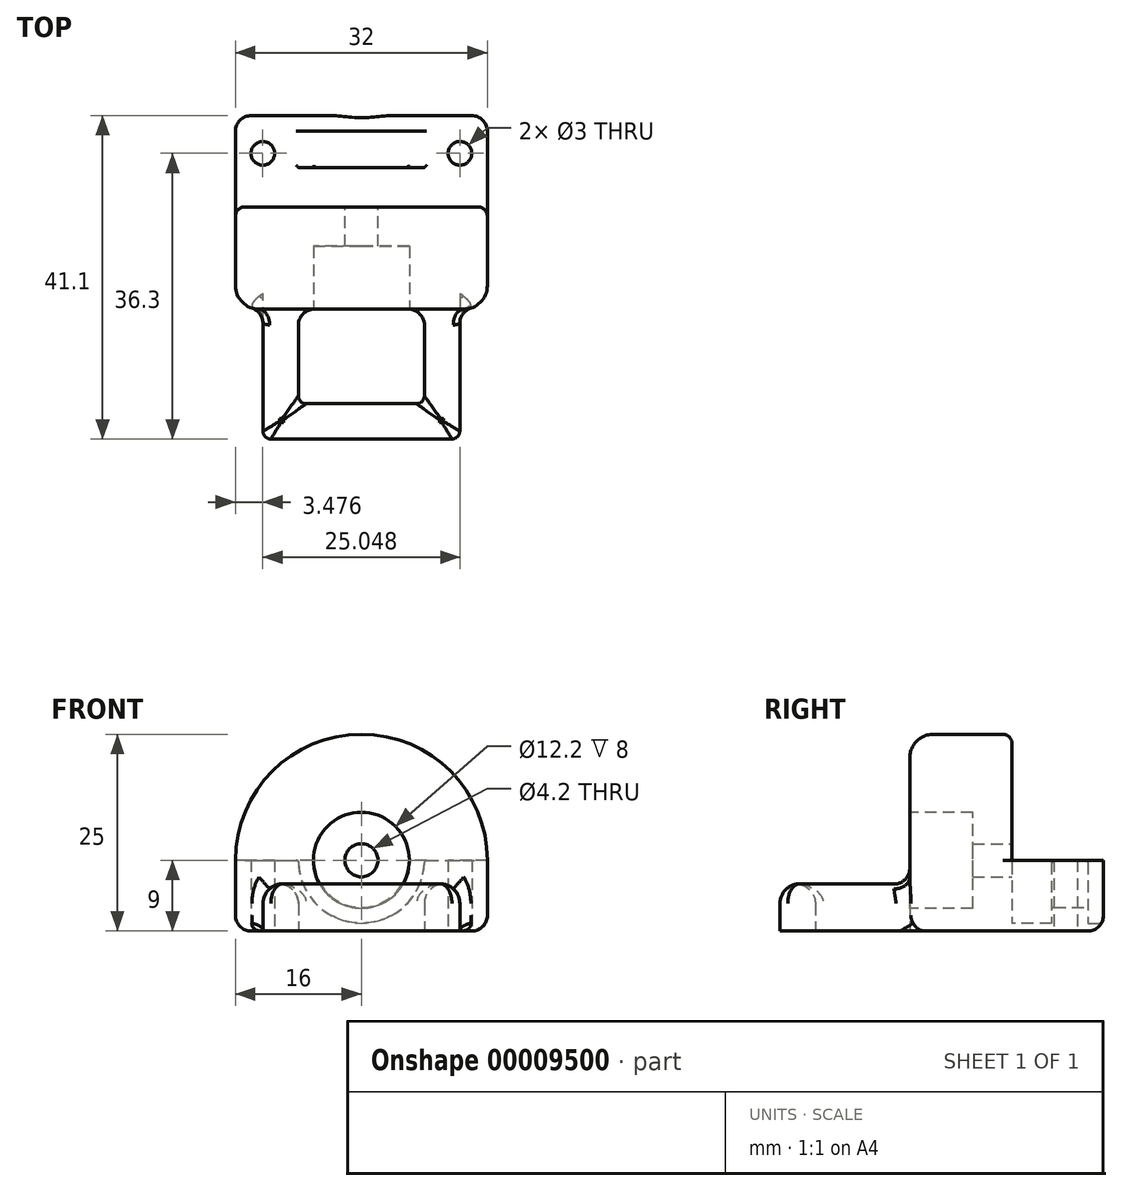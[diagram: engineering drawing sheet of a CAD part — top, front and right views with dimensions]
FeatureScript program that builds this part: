
annotation { "Feature Type Name" : "Feature", "Feature Type Description" : "" }
export const myFeature = defineFeature(function(context is Context, id is Id, definition is map)
    precondition{}
    {
        {
            var Q0;
            Q0=qCreatedBy(makeId("Top.planeOp"),FACE);
            var sketch = newSketch(context, id + "F0", { "sketchPlane" : qUnion([Q0])});
            skLineSegment(sketch, "E0.rect.bottom", {"start": v(-16, 5.8) * mm, "end": v(16, 5.8) * mm});
            skLineSegment(sketch, "E0.rect.top", {"start": v(-16, -5.8) * mm, "end": v(16, -5.8) * mm});
            skLineSegment(sketch, "E0.rect.left", {"start": v(-16, 5.8) * mm, "end": v(-16, -5.8) * mm});
            skLineSegment(sketch, "E0.rect.right", {"start": v(16, 5.8) * mm, "end": v(16, -5.8) * mm});
            skPoint(sketch, "E0.rect.middle", {"position": v(0, 0) * mm});
            skCircle(sketch, "E1", {"center": v(12.52, 1) * mm, "radius": 1.5 * mm});
            skCircle(sketch, "E2", {"center": v(-12.52, 1) * mm, "radius": 1.5 * mm});
            skSolve(sketch);
        }
        {
            var Q0;
            Q0=makeQuery(id+"F0.imprint","IMPRINT",FACE,{"disambiguationData":[TD([[makeQuery(id+"F0.imprint","IMPRINT",EDGE,{"derivedFrom":sQuery(id+"F0.wireOp",EDGE,"E0.rect.bottom")}),-1.0]])]});
            extrude(context, id + "F1", {"entities" : qUnion([Q0]), "depth" : 9 * mm});
        }
        {
            var Q0;
            Q0=makeQuery(id+"F1.opExtrude","SWEPT_FACE",FACE,{"disambiguationData":[OSD([sQuery(id+"F0.wireOp",EDGE,"E0.rect.top")])]});
            var sketch = newSketch(context, id + "F2", { "sketchPlane" : qUnion([Q0])});
            skCircle(sketch, "E3", {"center": v(0, 9) * mm, "radius": 8 * mm});
            skSolve(sketch);
        }
        {
            var Q0;
            Q0=qSketchRegion(id+"F2",true);
            var Q1;
            Q1=makeQuery(id+"F1.opExtrude","SWEPT_FACE",FACE,{"disambiguationData":[OSD([sQuery(id+"F0.wireOp",EDGE,"E0.rect.bottom")])]});
            extrude(context, id + "F3", {"entities" : qUnion([Q0, Q1]), "operationType" : NewBodyOperationType.REMOVE, "oppositeDirection" : true, "depth" : 5 * mm});
        }
        {
            var Q0;
            Q0=makeQuery(id+"F1.opExtrude","SWEPT_FACE",FACE,{"disambiguationData":[OSD([sQuery(id+"F0.wireOp",EDGE,"E0.rect.bottom")])]});
            var sketch = newSketch(context, id + "F4", { "sketchPlane" : qUnion([Q0])});
            skCircle(sketch, "E4", {"center": v(0, 9) * mm, "radius": 8 * mm});
            skSolve(sketch);
        }
        {
            var Q0;
            Q0=qSketchRegion(id+"F4",true);
            extrude(context, id + "F5", {"entities" : qUnion([Q0]), "operationType" : NewBodyOperationType.REMOVE, "oppositeDirection" : true, "depth" : 2 * mm});
        }
        {
            var Q0;
            Q0=makeQuery(id+"F5.boolean.opBoolean","COPY",FACE,{"derivedFrom":makeQuery(id+"F5.opExtrude","CAP_FACE",FACE,{"disambiguationData":[OSD([sQuery(id+"F4.wireOp",EDGE,"E4")])],"isStart":false})});
            var sketch = newSketch(context, id + "F6", { "sketchPlane" : qUnion([Q0])});
            skCircle(sketch, "E5", {"center": v(0, 9) * mm, "radius": 6 * mm});
            skSolve(sketch);
        }
        {
            var Q0;
            Q0=qSketchRegion(id+"F6",true);
            extrude(context, id + "F7", {"entities" : qUnion([Q0]), "operationType" : NewBodyOperationType.REMOVE, "oppositeDirection" : true, "depth" : 25 * mm});
        }
        {
            var Q0;
            Q0=makeQuery(id+"F1.opExtrude","SWEPT_FACE",FACE,{"disambiguationData":[OSD([sQuery(id+"F0.wireOp",EDGE,"E0.rect.top")])]});
            var sketch = newSketch(context, id + "F8", { "sketchPlane" : qUnion([Q0])});
            skArc(sketch, "E6", {"start": v(16, 9) * mm, "mid": v(0, 25) * mm, "end": v(-16, 9) * mm});
            skLineSegment(sketch, "E7", {"start": v(0, 0) * mm, "end": v(13.23, 0) * mm});
            skLineSegment(sketch, "E8", {"start": v(-13.23, 0) * mm, "end": v(0, 0) * mm});
            skLineSegment(sketch, "E9", {"start": v(-16, 9) * mm, "end": v(-16, 0) * mm});
            skLineSegment(sketch, "E10", {"start": v(16, 9) * mm, "end": v(16, 0) * mm});
            skLineSegment(sketch, "E11", {"start": v(-16, 0) * mm, "end": v(16, 0) * mm});
            skSolve(sketch);
        }
        {
            var Q0;
            Q0=qSketchRegion(id+"F8",true);
            extrude(context, id + "F9", {"entities" : qUnion([Q0]), "operationType" : NewBodyOperationType.ADD, "depth" : 13 * mm});
        }
        {
            var Q0;
            Q0=qCreatedBy(makeId("Top.planeOp"),FACE);
            var sketch = newSketch(context, id + "F10", { "sketchPlane" : qUnion([Q0])});
            skLineSegment(sketch, "E12", {"start": v(-8, -18.8) * mm, "end": v(-12.5, -18.8) * mm});
            skLineSegment(sketch, "E13", {"start": v(-12.5, -18.8) * mm, "end": v(-8, -18.8) * mm});
            skLineSegment(sketch, "E14", {"start": v(12.5, -18.8) * mm, "end": v(12.5, -35.3) * mm});
            skLineSegment(sketch, "E15", {"start": v(12.5, -35.3) * mm, "end": v(-12.5, -35.3) * mm});
            skLineSegment(sketch, "E16", {"start": v(-12.5, -35.3) * mm, "end": v(-12.5, -18.8) * mm});
            skLineSegment(sketch, "E17", {"start": v(-8, -18.8) * mm, "end": v(-8, -30.8) * mm});
            skLineSegment(sketch, "E18", {"start": v(-8, -30.8) * mm, "end": v(8, -30.8) * mm});
            skLineSegment(sketch, "E19", {"start": v(8, -30.8) * mm, "end": v(8, -18.8) * mm});
            skLineSegment(sketch, "E20.trimOffspring", {"start": v(8, -18.8) * mm, "end": v(12.5, -18.8) * mm});
            skPoint(sketch, "E21.orphan", {"position": v(0, -18.8) * mm});
            skPoint(sketch, "E22", {"position": v(0, -30.8) * mm});
            skPoint(sketch, "E23", {"position": v(0, -35.3) * mm});
            skSolve(sketch);
        }
        {
            var Q0;
            Q0=qSketchRegion(id+"F10",true);
            extrude(context, id + "F11", {"entities" : qUnion([Q0]), "operationType" : NewBodyOperationType.ADD, "depth" : 6 * mm});
        }
        {
            var Q0;
            Q0=makeQuery(id+"F11.opExtrude","CAP_EDGE",EDGE,{"disambiguationData":[OSD([sQuery(id+"F10.wireOp",EDGE,"E17")])],"isStart":false});
            var Q1;
            Q1=makeQuery(id+"F11.opExtrude","CAP_EDGE",EDGE,{"disambiguationData":[OSD([sQuery(id+"F10.wireOp",EDGE,"E16")])],"isStart":false});
            var Q2;
            Q2=makeQuery(id+"F11.opExtrude","CAP_EDGE",EDGE,{"disambiguationData":[OSD([sQuery(id+"F10.wireOp",EDGE,"E19")])],"isStart":false});
            var Q3;
            Q3=makeQuery(id+"F11.opExtrude","CAP_EDGE",EDGE,{"disambiguationData":[OSD([sQuery(id+"F10.wireOp",EDGE,"E14")])],"isStart":false});
            var Q4;
            Q4=makeQuery(id+"F11.opExtrude","CAP_EDGE",EDGE,{"disambiguationData":[OSD([sQuery(id+"F10.wireOp",EDGE,"E18")])],"isStart":false});
            var Q5;
            Q5=makeQuery(id+"F11.opExtrude","CAP_EDGE",EDGE,{"disambiguationData":[OSD([sQuery(id+"F10.wireOp",EDGE,"E15")])],"isStart":false});
            fillet(context, id + "F12", {"entities" : qUnion([Q0, Q1, Q2, Q3, Q4, Q5]), "radius" : 2.5 * mm, "tangentPropagation" : true, "allowEdgeOverflow" : false});
        }
        {
            var Q0;
            Q0=makeQuery(id+"F9.opExtrude","CAP_EDGE",EDGE,{"disambiguationData":[OSD([sQuery(id+"F8.wireOp",EDGE,"E6")])],"isStart":false});
            fillet(context, id + "F13", {"entities" : qUnion([Q0]), "radius" : 3 * mm, "tangentPropagation" : true, "allowEdgeOverflow" : false});
        }
        {
            var Q0;
            Q0=makeQuery(id+"F9.opExtrude","CAP_EDGE",EDGE,{"disambiguationData":[OSD([sQuery(id+"F8.wireOp",EDGE,"E6")])],"isStart":true});
            fillet(context, id + "F14", {"entities" : qUnion([Q0]), "radius" : 1.2 * mm, "tangentPropagation" : true, "allowEdgeOverflow" : false});
        }
        {
            var Q0;
            Q0=makeQuery(id+"F9.opExtrude","CAP_FACE",FACE,{"disambiguationData":[OSD([sQuery(id+"F8.wireOp",EDGE,"E6"),sQuery(id+"F8.wireOp",EDGE,"E9"),sQuery(id+"F8.wireOp",EDGE,"E10"),sQuery(id+"F8.wireOp",EDGE,"E11")])],"isStart":false});
            var sketch = newSketch(context, id + "F15", { "sketchPlane" : qUnion([Q0])});
            skCircle(sketch, "E24", {"center": v(0, 9) * mm, "radius": 6.1 * mm});
            skSolve(sketch);
        }
        {
            var Q0;
            Q0=qSketchRegion(id+"F15",true);
            extrude(context, id + "F16", {"entities" : qUnion([Q0]), "operationType" : NewBodyOperationType.REMOVE, "oppositeDirection" : true, "depth" : 8 * mm});
        }
        {
            var Q0;
            Q0=makeQuery(id+"F13.opFillet","BLEND_EDGE",EDGE,{"blendedFrom":[makeQuery(id+"F9.opExtrude","CAP_EDGE",EDGE,{"disambiguationData":[OSD([sQuery(id+"F8.wireOp",EDGE,"E9")])],"isStart":false}),makeQuery(id+"F9.boolean.opBoolean","MERGE",FACE,{"derivedFrom":[makeQuery(id+"F1.opExtrude","CAP_FACE",FACE,{"disambiguationData":[OSD([sQuery(id+"F0.wireOp",EDGE,"E0.rect.bottom"),sQuery(id+"F0.wireOp",EDGE,"E0.rect.top"),sQuery(id+"F0.wireOp",EDGE,"E0.rect.left"),sQuery(id+"F0.wireOp",EDGE,"E0.rect.right"),sQuery(id+"F0.wireOp",EDGE,"E1"),sQuery(id+"F0.wireOp",EDGE,"E2")])],"isStart":true}),makeQuery(id+"F9.opExtrude","SWEPT_FACE",FACE,{"disambiguationData":[OSD([sQuery(id+"F8.wireOp",EDGE,"E11")])]})]})],"blendedInto":[makeQuery(id+"F9.boolean.opBoolean","MERGE",FACE,{"derivedFrom":[makeQuery(id+"F1.opExtrude","CAP_FACE",FACE,{"disambiguationData":[OSD([sQuery(id+"F0.wireOp",EDGE,"E0.rect.bottom"),sQuery(id+"F0.wireOp",EDGE,"E0.rect.top"),sQuery(id+"F0.wireOp",EDGE,"E0.rect.left"),sQuery(id+"F0.wireOp",EDGE,"E0.rect.right"),sQuery(id+"F0.wireOp",EDGE,"E1"),sQuery(id+"F0.wireOp",EDGE,"E2")])],"isStart":true}),makeQuery(id+"F9.opExtrude","SWEPT_FACE",FACE,{"disambiguationData":[OSD([sQuery(id+"F8.wireOp",EDGE,"E11")])]})]})]});
            fillet(context, id + "F17", {"entities" : qUnion([Q0]), "radius" : 2 * mm, "tangentPropagation" : true, "allowEdgeOverflow" : false});
        }
        {
            var Q0;
            {var subQ0=sQuery(id+"F8.wireOp",EDGE,"E6");var subQ1=sQuery(id+"F8.wireOp",EDGE,"E9");var subQ2=sQuery(id+"F8.wireOp",EDGE,"E10");Q0=makeQuery(id+"F9.boolean.opBoolean","SPLIT",FACE,{"disambiguationData":[TD([makeQuery(id+"F3.boolean.opBoolean","COPY",FACE,{"derivedFrom":makeQuery(id+"F3.opExtrude","SWEPT_FACE",FACE,{"disambiguationData":[OSD([sQuery(id+"F2.wireOp",EDGE,"E3")])]})})])],"derivedFrom":makeQuery(id+"F9.opExtrude","CAP_FACE",FACE,{"disambiguationData":[OSD([subQ0,subQ1,subQ2,sQuery(id+"F8.wireOp",EDGE,"E11")])],"isStart":true})});}
            var sketch = newSketch(context, id + "F18", { "sketchPlane" : qUnion([Q0])});
            skCircle(sketch, "E25", {"center": v(0, 9) * mm, "radius": 2.1 * mm});
            skSolve(sketch);
        }
        {
            var Q0;
            Q0=makeQuery(id+"F1.opExtrude","CAP_EDGE",EDGE,{"disambiguationData":[OSD([sQuery(id+"F0.wireOp",EDGE,"E0.rect.bottom")])],"isStart":true});
            var Q1;
            Q1=makeQuery(id+"F7.boolean.opBoolean","COPY",EDGE,{"derivedFrom":makeQuery(id+"F7.opExtrude","CAP_EDGE",EDGE,{"disambiguationData":[OSD([sQuery(id+"F6.wireOp",EDGE,"E5")])],"isStart":true})});
            var Q2;
            Q2=makeQuery(id+"F1.opExtrude","SWEPT_EDGE",EDGE,{"disambiguationData":[OSD([sQuery(id+"F0.wireOp",EDGE,"E0.rect.bottom"),sQuery(id+"F0.wireOp",EDGE,"E0.rect.left")])]});
            var Q3;
            Q3=makeQuery(id+"F1.opExtrude","CAP_EDGE",EDGE,{"disambiguationData":[OSD([sQuery(id+"F0.wireOp",EDGE,"E0.rect.left")])],"isStart":true});
            var Q4;
            Q4=makeQuery(id+"F1.opExtrude","SWEPT_EDGE",EDGE,{"disambiguationData":[OSD([sQuery(id+"F0.wireOp",EDGE,"E0.rect.bottom"),sQuery(id+"F0.wireOp",EDGE,"E0.rect.right")])]});
            var Q5;
            Q5=makeQuery(id+"F1.opExtrude","CAP_EDGE",EDGE,{"disambiguationData":[OSD([sQuery(id+"F0.wireOp",EDGE,"E0.rect.right")])],"isStart":true});
            fillet(context, id + "F19", {"entities" : qUnion([Q0, Q1, Q2, Q3, Q4, Q5]), "radius" : 2 * mm, "tangentPropagation" : true, "allowEdgeOverflow" : false});
        }
        {
            var Q0;
            Q0 = qSketchRegion(id + "F18", true);
            extrude(context, id + "F20", {"entities" : qUnion([Q0]), "operationType" : NewBodyOperationType.REMOVE, "oppositeDirection" : true, "depth" : 7 * mm});
        }
        {
            var Q0;
            Q0=makeQuery(id+"F12.opFillet","BLEND_EDGE",EDGE,{"blendedFrom":[makeQuery(id+"F11.opExtrude","CAP_EDGE",EDGE,{"disambiguationData":[OSD([sQuery(id+"F10.wireOp",EDGE,"E14")])],"isStart":false}),makeQuery(id+"F11.opExtrude","CAP_EDGE",EDGE,{"disambiguationData":[OSD([sQuery(id+"F10.wireOp",EDGE,"E15")])],"isStart":false})],"blendedInto":[]});
            var Q1;
            Q1=makeQuery(id+"F12.opFillet","BLEND_EDGE",EDGE,{"blendedFrom":[makeQuery(id+"F11.opExtrude","CAP_EDGE",EDGE,{"disambiguationData":[OSD([sQuery(id+"F10.wireOp",EDGE,"E18")])],"isStart":false}),makeQuery(id+"F11.opExtrude","CAP_EDGE",EDGE,{"disambiguationData":[OSD([sQuery(id+"F10.wireOp",EDGE,"E19")])],"isStart":false})],"blendedInto":[]});
            var Q2;
            Q2=makeQuery(id+"F12.opFillet","BLEND_EDGE",EDGE,{"blendedFrom":[makeQuery(id+"F11.opExtrude","CAP_EDGE",EDGE,{"disambiguationData":[OSD([sQuery(id+"F10.wireOp",EDGE,"E14")])],"isStart":false}),makeQuery(id+"F11.opExtrude","CAP_EDGE",EDGE,{"disambiguationData":[OSD([sQuery(id+"F10.wireOp",EDGE,"E19")])],"isStart":false})],"blendedInto":[]});
            var Q3;
            Q3=makeQuery(id+"F12.opFillet","BLEND_EDGE",EDGE,{"blendedFrom":[makeQuery(id+"F11.opExtrude","CAP_EDGE",EDGE,{"disambiguationData":[OSD([sQuery(id+"F10.wireOp",EDGE,"E15")])],"isStart":false}),makeQuery(id+"F11.opExtrude","CAP_EDGE",EDGE,{"disambiguationData":[OSD([sQuery(id+"F10.wireOp",EDGE,"E18")])],"isStart":false})],"blendedInto":[]});
            var Q4;
            Q4=makeQuery(id+"F12.opFillet","BLEND_EDGE",EDGE,{"blendedFrom":[makeQuery(id+"F11.opExtrude","CAP_EDGE",EDGE,{"disambiguationData":[OSD([sQuery(id+"F10.wireOp",EDGE,"E16")])],"isStart":false}),makeQuery(id+"F11.opExtrude","CAP_EDGE",EDGE,{"disambiguationData":[OSD([sQuery(id+"F10.wireOp",EDGE,"E17")])],"isStart":false})],"blendedInto":[]});
            var Q5;
            Q5=makeQuery(id+"F12.opFillet","BLEND_EDGE",EDGE,{"blendedFrom":[makeQuery(id+"F11.opExtrude","CAP_EDGE",EDGE,{"disambiguationData":[OSD([sQuery(id+"F10.wireOp",EDGE,"E15")])],"isStart":false}),makeQuery(id+"F11.opExtrude","CAP_EDGE",EDGE,{"disambiguationData":[OSD([sQuery(id+"F10.wireOp",EDGE,"E16")])],"isStart":false})],"blendedInto":[]});
            var Q6;
            Q6=makeQuery(id+"F12.opFillet","BLEND_EDGE",EDGE,{"blendedFrom":[makeQuery(id+"F11.opExtrude","CAP_EDGE",EDGE,{"disambiguationData":[OSD([sQuery(id+"F10.wireOp",EDGE,"E17")])],"isStart":false}),makeQuery(id+"F11.opExtrude","CAP_EDGE",EDGE,{"disambiguationData":[OSD([sQuery(id+"F10.wireOp",EDGE,"E18")])],"isStart":false})],"blendedInto":[]});
            fillet(context, id + "F21", {"entities" : qUnion([Q0, Q1, Q2, Q3, Q4, Q5, Q6]), "radius" : 1 * mm, "tangentPropagation" : true, "allowEdgeOverflow" : false});
        }
        {
            var Q0;
            Q0=makeQuery(id+"F12.opFillet","BLEND_EDGE",EDGE,{"blendedFrom":[makeQuery(id+"F11.opExtrude","CAP_EDGE",EDGE,{"disambiguationData":[OSD([sQuery(id+"F10.wireOp",EDGE,"E14")])],"isStart":false}),makeQuery(id+"F9.opExtrude","CAP_FACE",FACE,{"disambiguationData":[OSD([sQuery(id+"F8.wireOp",EDGE,"E6"),sQuery(id+"F8.wireOp",EDGE,"E9"),sQuery(id+"F8.wireOp",EDGE,"E10"),sQuery(id+"F8.wireOp",EDGE,"E11")])],"isStart":false})],"blendedInto":[makeQuery(id+"F9.opExtrude","CAP_FACE",FACE,{"disambiguationData":[OSD([sQuery(id+"F8.wireOp",EDGE,"E6"),sQuery(id+"F8.wireOp",EDGE,"E9"),sQuery(id+"F8.wireOp",EDGE,"E10"),sQuery(id+"F8.wireOp",EDGE,"E11")])],"isStart":false})]});
            var Q1;
            Q1=makeQuery(id+"F12.opFillet","BLEND_EDGE",EDGE,{"blendedFrom":[makeQuery(id+"F11.opExtrude","CAP_EDGE",EDGE,{"disambiguationData":[OSD([sQuery(id+"F10.wireOp",EDGE,"E17")])],"isStart":false}),makeQuery(id+"F9.opExtrude","CAP_FACE",FACE,{"disambiguationData":[OSD([sQuery(id+"F8.wireOp",EDGE,"E6"),sQuery(id+"F8.wireOp",EDGE,"E9"),sQuery(id+"F8.wireOp",EDGE,"E10"),sQuery(id+"F8.wireOp",EDGE,"E11")])],"isStart":false})],"blendedInto":[makeQuery(id+"F9.opExtrude","CAP_FACE",FACE,{"disambiguationData":[OSD([sQuery(id+"F8.wireOp",EDGE,"E6"),sQuery(id+"F8.wireOp",EDGE,"E9"),sQuery(id+"F8.wireOp",EDGE,"E10"),sQuery(id+"F8.wireOp",EDGE,"E11")])],"isStart":false})]});
            fillet(context, id + "F22", {"entities" : qUnion([Q0, Q1]), "radius" : 2 * mm, "tangentPropagation" : true, "allowEdgeOverflow" : false});
        }
        {
            var Q0;
            Q0=makeQuery(id+"F3.boolean.opBoolean","INTERSECT",EDGE,{"disambiguationData":[OD(0.0)],"derivedFrom":[makeQuery(id+"F1.opExtrude","CAP_FACE",FACE,{"disambiguationData":[OSD([sQuery(id+"F0.wireOp",EDGE,"E0.rect.bottom"),sQuery(id+"F0.wireOp",EDGE,"E0.rect.top"),sQuery(id+"F0.wireOp",EDGE,"E0.rect.left"),sQuery(id+"F0.wireOp",EDGE,"E0.rect.right"),sQuery(id+"F0.wireOp",EDGE,"E1"),sQuery(id+"F0.wireOp",EDGE,"E2")])],"isStart":false}),makeQuery(id+"F3.opExtrude","SWEPT_FACE",FACE,{"disambiguationData":[OSD([sQuery(id+"F2.wireOp",EDGE,"E3")])]})]});
            var Q1;
            Q1=makeQuery(id+"F3.boolean.opBoolean","INTERSECT",EDGE,{"disambiguationData":[OD(1.0)],"derivedFrom":[makeQuery(id+"F1.opExtrude","CAP_FACE",FACE,{"disambiguationData":[OSD([sQuery(id+"F0.wireOp",EDGE,"E0.rect.bottom"),sQuery(id+"F0.wireOp",EDGE,"E0.rect.top"),sQuery(id+"F0.wireOp",EDGE,"E0.rect.left"),sQuery(id+"F0.wireOp",EDGE,"E0.rect.right"),sQuery(id+"F0.wireOp",EDGE,"E1"),sQuery(id+"F0.wireOp",EDGE,"E2")])],"isStart":false}),makeQuery(id+"F3.opExtrude","SWEPT_FACE",FACE,{"disambiguationData":[OSD([sQuery(id+"F2.wireOp",EDGE,"E3")])]})]});
            var Q2;
            Q2=makeQuery(id+"F7.boolean.opBoolean","INTERSECT",EDGE,{"disambiguationData":[OD(1.0)],"derivedFrom":[makeQuery(id+"F1.opExtrude","CAP_FACE",FACE,{"disambiguationData":[OSD([sQuery(id+"F0.wireOp",EDGE,"E0.rect.bottom"),sQuery(id+"F0.wireOp",EDGE,"E0.rect.top"),sQuery(id+"F0.wireOp",EDGE,"E0.rect.left"),sQuery(id+"F0.wireOp",EDGE,"E0.rect.right"),sQuery(id+"F0.wireOp",EDGE,"E1"),sQuery(id+"F0.wireOp",EDGE,"E2")])],"isStart":false}),makeQuery(id+"F7.opExtrude","SWEPT_FACE",FACE,{"disambiguationData":[OSD([sQuery(id+"F6.wireOp",EDGE,"E5")])]})]});
            var Q3;
            Q3=makeQuery(id+"F7.boolean.opBoolean","INTERSECT",EDGE,{"disambiguationData":[OD(0.0)],"derivedFrom":[makeQuery(id+"F1.opExtrude","CAP_FACE",FACE,{"disambiguationData":[OSD([sQuery(id+"F0.wireOp",EDGE,"E0.rect.bottom"),sQuery(id+"F0.wireOp",EDGE,"E0.rect.top"),sQuery(id+"F0.wireOp",EDGE,"E0.rect.left"),sQuery(id+"F0.wireOp",EDGE,"E0.rect.right"),sQuery(id+"F0.wireOp",EDGE,"E1"),sQuery(id+"F0.wireOp",EDGE,"E2")])],"isStart":false}),makeQuery(id+"F7.opExtrude","SWEPT_FACE",FACE,{"disambiguationData":[OSD([sQuery(id+"F6.wireOp",EDGE,"E5")])]})]});
            var Q4;
            Q4=makeQuery(id+"F5.boolean.opBoolean","INTERSECT",EDGE,{"disambiguationData":[OD(1.0)],"derivedFrom":[makeQuery(id+"F1.opExtrude","CAP_FACE",FACE,{"disambiguationData":[OSD([sQuery(id+"F0.wireOp",EDGE,"E0.rect.bottom"),sQuery(id+"F0.wireOp",EDGE,"E0.rect.top"),sQuery(id+"F0.wireOp",EDGE,"E0.rect.left"),sQuery(id+"F0.wireOp",EDGE,"E0.rect.right"),sQuery(id+"F0.wireOp",EDGE,"E1"),sQuery(id+"F0.wireOp",EDGE,"E2")])],"isStart":false}),makeQuery(id+"F5.opExtrude","SWEPT_FACE",FACE,{"disambiguationData":[OSD([sQuery(id+"F4.wireOp",EDGE,"E4")])]})]});
            var Q5;
            Q5=makeQuery(id+"F5.boolean.opBoolean","INTERSECT",EDGE,{"disambiguationData":[OD(0.0)],"derivedFrom":[makeQuery(id+"F1.opExtrude","CAP_FACE",FACE,{"disambiguationData":[OSD([sQuery(id+"F0.wireOp",EDGE,"E0.rect.bottom"),sQuery(id+"F0.wireOp",EDGE,"E0.rect.top"),sQuery(id+"F0.wireOp",EDGE,"E0.rect.left"),sQuery(id+"F0.wireOp",EDGE,"E0.rect.right"),sQuery(id+"F0.wireOp",EDGE,"E1"),sQuery(id+"F0.wireOp",EDGE,"E2")])],"isStart":false}),makeQuery(id+"F5.opExtrude","SWEPT_FACE",FACE,{"disambiguationData":[OSD([sQuery(id+"F4.wireOp",EDGE,"E4")])]})]});
            var Q6;
            Q6=makeQuery(id+"F7.boolean.opBoolean","INTERSECT",EDGE,{"derivedFrom":[makeQuery(id+"F3.boolean.opBoolean","COPY",FACE,{"derivedFrom":makeQuery(id+"F3.opExtrude","CAP_FACE",FACE,{"disambiguationData":[OSD([sQuery(id+"F2.wireOp",EDGE,"E3")])],"isStart":false})}),makeQuery(id+"F7.opExtrude","SWEPT_FACE",FACE,{"disambiguationData":[OSD([sQuery(id+"F6.wireOp",EDGE,"E5")])]})]});
            var Q7;
            Q7=makeQuery(id+"F7.boolean.opBoolean","SPLIT",EDGE,{"disambiguationData":[OD(0.0)],"derivedFrom":makeQuery(id+"F3.boolean.opBoolean","INTERSECT",EDGE,{"derivedFrom":[makeQuery(id+"F1.opExtrude","CAP_FACE",FACE,{"disambiguationData":[OSD([sQuery(id+"F0.wireOp",EDGE,"E0.rect.bottom"),sQuery(id+"F0.wireOp",EDGE,"E0.rect.top"),sQuery(id+"F0.wireOp",EDGE,"E0.rect.left"),sQuery(id+"F0.wireOp",EDGE,"E0.rect.right"),sQuery(id+"F0.wireOp",EDGE,"E1"),sQuery(id+"F0.wireOp",EDGE,"E2")])],"isStart":false}),makeQuery(id+"F3.opExtrude","CAP_FACE",FACE,{"disambiguationData":[OSD([sQuery(id+"F2.wireOp",EDGE,"E3")])],"isStart":false})]})});
            var Q8;
            Q8=makeQuery(id+"F7.boolean.opBoolean","SPLIT",EDGE,{"disambiguationData":[OD(1.0)],"derivedFrom":makeQuery(id+"F3.boolean.opBoolean","INTERSECT",EDGE,{"derivedFrom":[makeQuery(id+"F1.opExtrude","CAP_FACE",FACE,{"disambiguationData":[OSD([sQuery(id+"F0.wireOp",EDGE,"E0.rect.bottom"),sQuery(id+"F0.wireOp",EDGE,"E0.rect.top"),sQuery(id+"F0.wireOp",EDGE,"E0.rect.left"),sQuery(id+"F0.wireOp",EDGE,"E0.rect.right"),sQuery(id+"F0.wireOp",EDGE,"E1"),sQuery(id+"F0.wireOp",EDGE,"E2")])],"isStart":false}),makeQuery(id+"F3.opExtrude","CAP_FACE",FACE,{"disambiguationData":[OSD([sQuery(id+"F2.wireOp",EDGE,"E3")])],"isStart":false})]})});
            var Q9;
            Q9=makeQuery(id+"F20.boolean.opBoolean","COPY",EDGE,{"derivedFrom":makeQuery(id+"F20.opExtrude","CAP_EDGE",EDGE,{"disambiguationData":[OSD([sQuery(id+"F18.wireOp",EDGE,"E25")])],"isStart":true})});
            fillet(context, id + "F23", {"entities" : qUnion([Q0, Q1, Q2, Q3, Q4, Q5, Q6, Q7, Q8, Q9]), "radius" : 0.3 * mm, "allowEdgeOverflow" : false});
        }
    });
